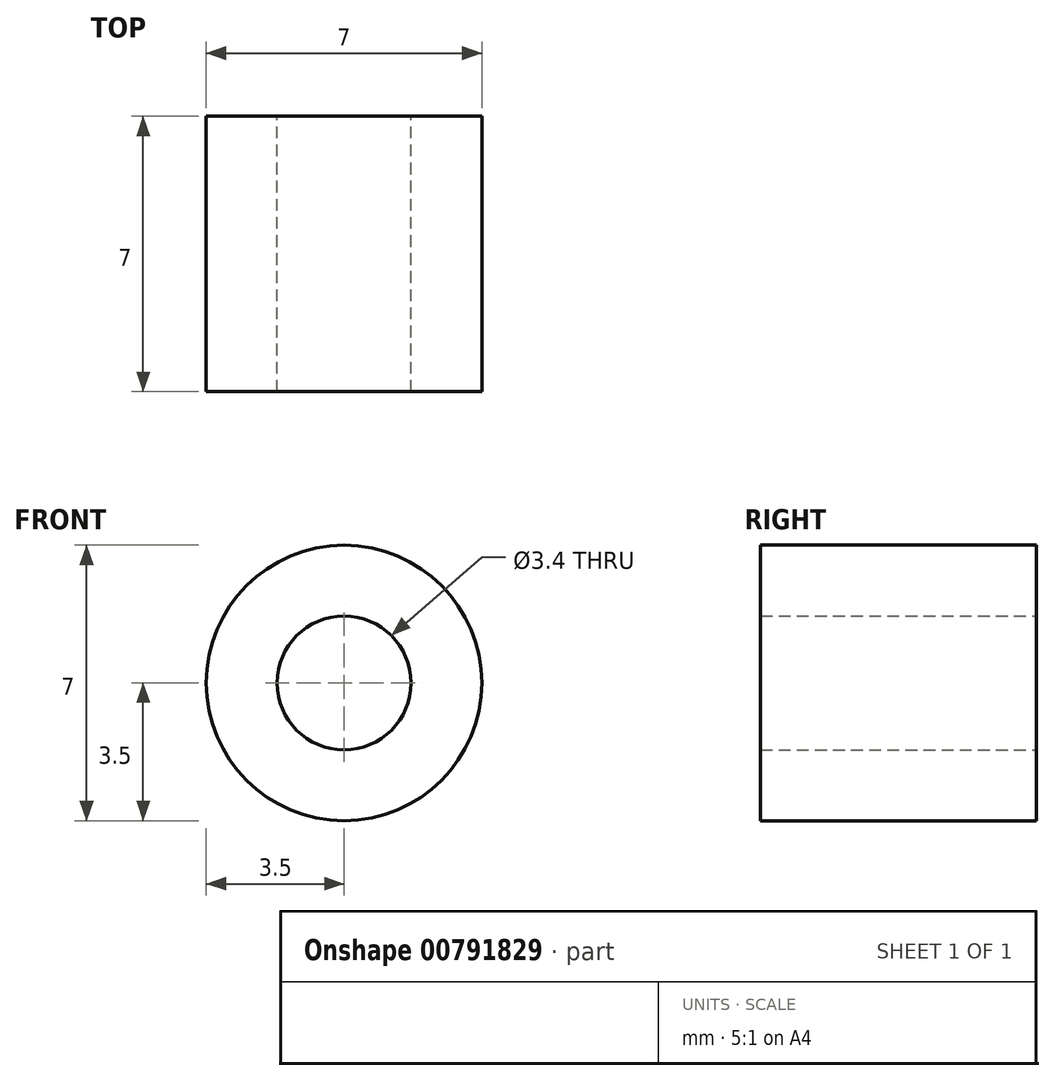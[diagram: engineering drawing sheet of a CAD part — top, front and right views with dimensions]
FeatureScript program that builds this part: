
annotation { "Feature Type Name" : "Feature", "Feature Type Description" : "" }
export const myFeature = defineFeature(function(context is Context, id is Id, definition is map)
    precondition{}
    {
        {
            var Q0;
            Q0=qCreatedBy(makeId("Front.planeOp"),FACE);
            var sketch = newSketch(context, id + "F0", { "sketchPlane" : qUnion([Q0])});
            skCircle(sketch, "E0", {"center": v(0, 0) * mm, "radius": 3.5 * mm});
            skCircle(sketch, "E1", {"center": v(0, 0) * mm, "radius": 1.7 * mm});
            skSolve(sketch);
        }
        {
            var Q0;
            Q0 = qSketchRegion(id + "F0", true);
            var Q1;
            Q1=makeQuery(id+"F0.imprint","IMPRINT",FACE,{"disambiguationData":[TD([[makeQuery(id+"F0.imprint","IMPRINT",EDGE,{"derivedFrom":sQuery(id+"F0.wireOp",EDGE,"E0")}),1.0]])]});
            extrude(context, id + "F1", {"entities" : qUnion([Q0, Q1]), "depth" : 7 * mm, "offsetDistance" : 25 * mm});
        }
    });
